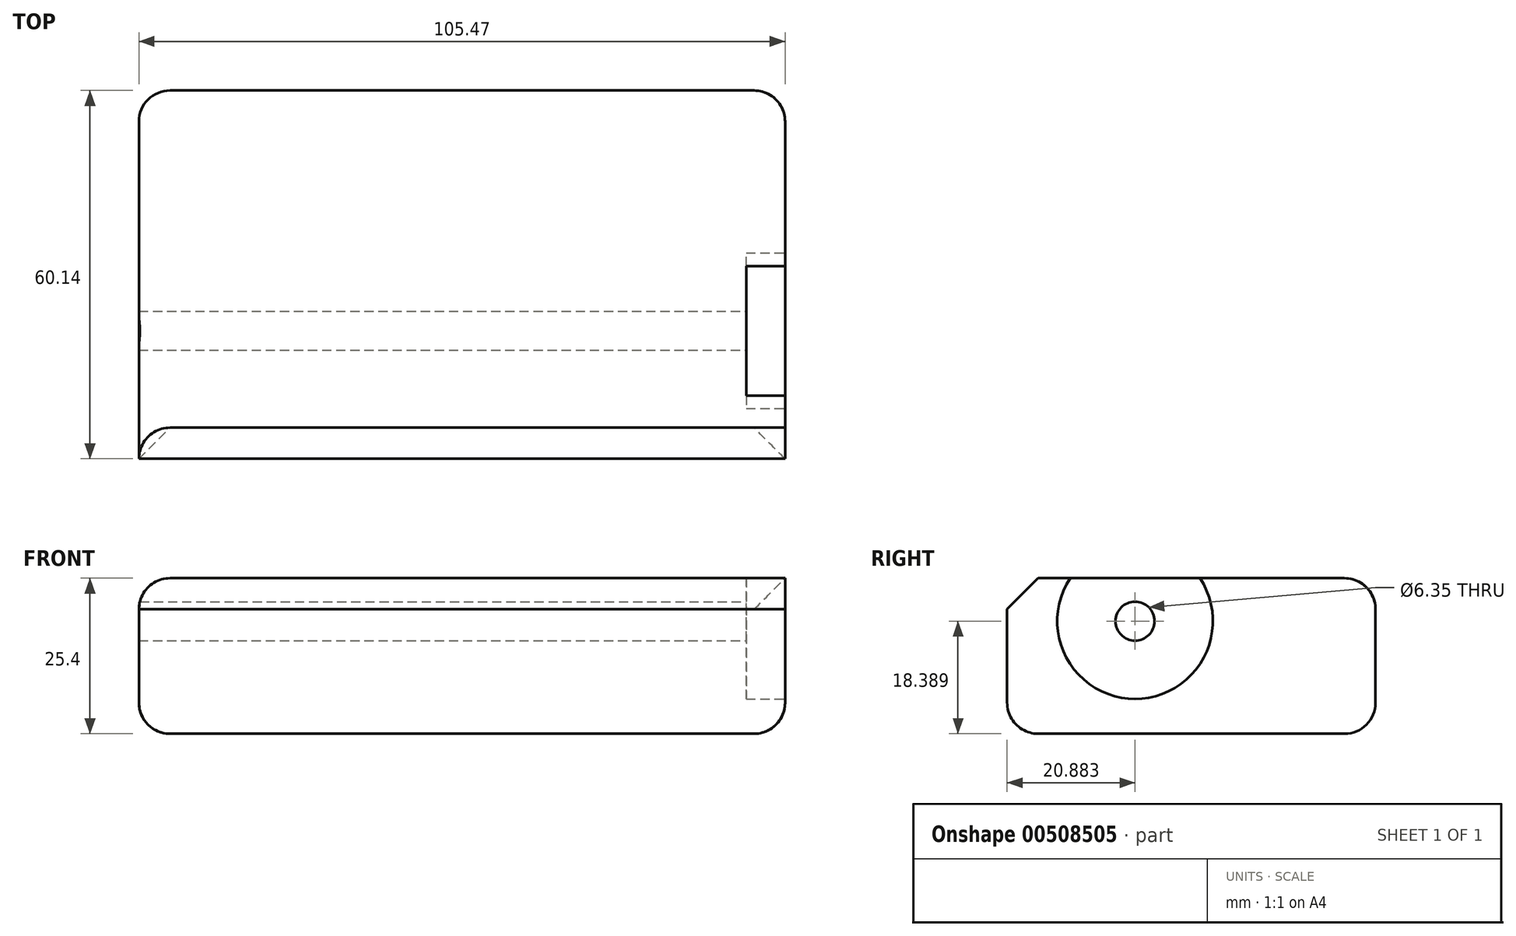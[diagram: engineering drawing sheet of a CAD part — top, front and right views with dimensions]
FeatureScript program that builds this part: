
annotation { "Feature Type Name" : "Feature", "Feature Type Description" : "" }
export const myFeature = defineFeature(function(context is Context, id is Id, definition is map)
    precondition{}
    {
        {
            var Q0;
            Q0=qCreatedBy(makeId("Top.planeOp"),FACE);
            var sketch = newSketch(context, id + "F0", { "sketchPlane" : qUnion([Q0])});
            skLineSegment(sketch, "E0.bottom", {"start": v(-50.38, 24.18) * mm, "end": v(55.1, 24.18) * mm});
            skLineSegment(sketch, "E0.top", {"start": v(-50.38, -35.96) * mm, "end": v(55.1, -35.96) * mm});
            skLineSegment(sketch, "E0.left", {"start": v(-50.38, 24.18) * mm, "end": v(-50.38, -35.96) * mm});
            skLineSegment(sketch, "E0.right", {"start": v(55.1, 24.18) * mm, "end": v(55.1, -35.96) * mm});
            skSolve(sketch);
        }
        {
            var Q0;
            Q0=makeQuery(id+"F0.imprint","IMPRINT",FACE,{"disambiguationData":[TD([[makeQuery(id+"F0.imprint","IMPRINT",EDGE,{"derivedFrom":sQuery(id+"F0.wireOp",EDGE,"E0.bottom")}),-1.0]])]});
            extrude(context, id + "F1", {"entities" : qUnion([Q0]), "depth" : 25.4 * mm});
        }
        {
            var Q0;
            Q0=makeQuery(id+"F1.opExtrude","CAP_EDGE",EDGE,{"disambiguationData":[OSD([sQuery(id+"F0.wireOp",EDGE,"E0.top")])],"isStart":false});
            chamfer(context, id + "F2", {"entities" : qUnion([Q0]), "width" : 5.08 * mm, "tangentPropagation" : true});
        }
        {
            var Q0;
            Q0=makeQuery(id+"F1.opExtrude","CAP_EDGE",EDGE,{"disambiguationData":[OSD([sQuery(id+"F0.wireOp",EDGE,"E0.left")])],"isStart":false});
            fillet(context, id + "F3", {"entities" : qUnion([Q0]), "radius" : 5.08 * mm, "tangentPropagation" : true, "allowEdgeOverflow" : false});
        }
        {
            var Q0;
            Q0=makeQuery(id+"F1.opExtrude","SWEPT_FACE",FACE,{"disambiguationData":[OSD([sQuery(id+"F0.wireOp",EDGE,"E0.right")])]});
            var sketch = newSketch(context, id + "F4", { "sketchPlane" : qUnion([Q0])});
            skCircle(sketch, "E1", {"center": v(-15.08, 18.39) * mm, "radius": 10.54 * mm});
            skSolve(sketch);
        }
        {
            var Q0;
            Q0=sQuery(id+"F4.wireOp",VERTEX,"E1.center");
            var Q1;
            Q1=makeQuery(id+"F1.opExtrude","SWEPT_BODY",BODY,{"disambiguationData":[OSD([sQuery(id+"F0.wireOp",EDGE,"E0.bottom"),sQuery(id+"F0.wireOp",EDGE,"E0.top"),sQuery(id+"F0.wireOp",EDGE,"E0.left"),sQuery(id+"F0.wireOp",EDGE,"E0.right")])]});
            hole(context, id + "F5", {"style" : HoleStyle.C_BORE, "endStyle" : HoleEndStyle.THROUGH, "holeDiameter" : 6.35 * mm, "cBoreDiameter" : 25.4 * mm, "cBoreDepth" : 6.35 * mm, "isTappedThrough" : true, "tappedDepth" : 12.7 * mm, "tapClearance" : 3, "locations" : qUnion([Q0]), "scope" : qUnion([Q1])});
        }
        {
            var Q0;
            Q0=makeQuery(id+"F1.opExtrude","SWEPT_FACE",FACE,{"disambiguationData":[OSD([sQuery(id+"F0.wireOp",EDGE,"E0.bottom")])]});
            var Q1;
            Q1=makeQuery(id+"F1.opExtrude","CAP_FACE",FACE,{"disambiguationData":[OSD([sQuery(id+"F0.wireOp",EDGE,"E0.bottom"),sQuery(id+"F0.wireOp",EDGE,"E0.top"),sQuery(id+"F0.wireOp",EDGE,"E0.left"),sQuery(id+"F0.wireOp",EDGE,"E0.right")])],"isStart":true});
            fillet(context, id + "F6", {"entities" : qUnion([Q0, Q1]), "radius" : 5.08 * mm, "tangentPropagation" : true, "allowEdgeOverflow" : false});
        }
    });
